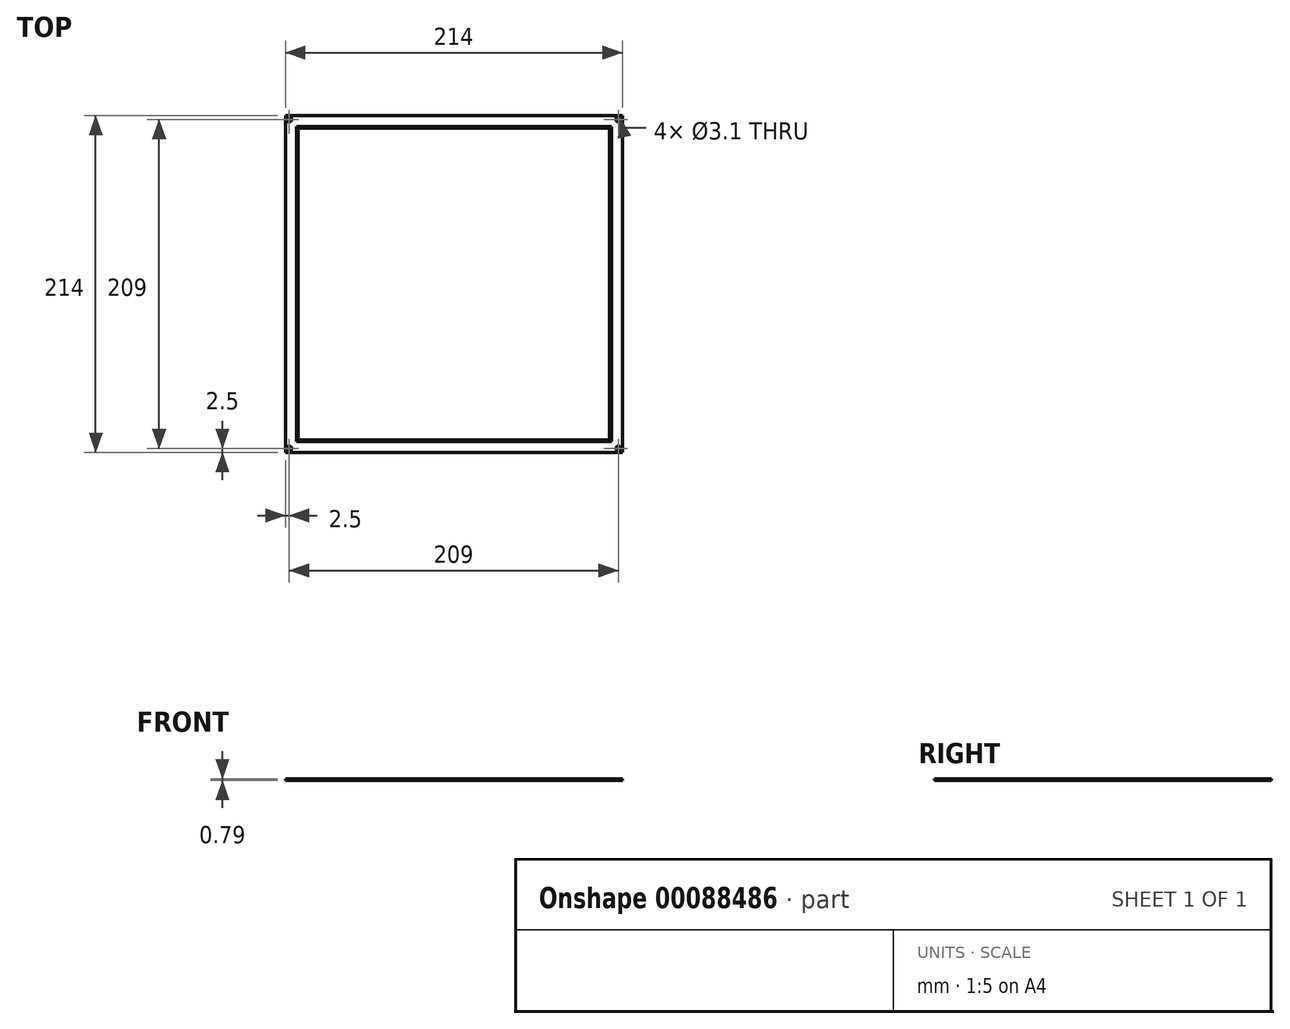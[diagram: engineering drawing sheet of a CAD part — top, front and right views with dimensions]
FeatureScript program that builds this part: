
annotation { "Feature Type Name" : "Feature", "Feature Type Description" : "" }
export const myFeature = defineFeature(function(context is Context, id is Id, definition is map)
    precondition{}
    {
        {
            var Q0;
            Q0=qCreatedBy(makeId("Top.planeOp"),FACE);
            var sketch = newSketch(context, id + "F0", { "sketchPlane" : qUnion([Q0])});
            skLineSegment(sketch, "E0.bottom", {"start": v(-107, 107) * mm, "end": v(107, 107) * mm});
            skLineSegment(sketch, "E0.top", {"start": v(-107, -107) * mm, "end": v(107, -107) * mm});
            skLineSegment(sketch, "E0.left", {"start": v(-107, 107) * mm, "end": v(-107, -107) * mm});
            skLineSegment(sketch, "E0.right", {"start": v(107, 107) * mm, "end": v(107, -107) * mm});
            skLineSegment(sketch, "E1", {"start": v(-107, 107) * mm, "end": v(107, -107) * mm, "construction": true});
            skLineSegment(sketch, "E2", {"start": v(107, 107) * mm, "end": v(-107, -107) * mm, "construction": true});
            skLineSegment(sketch, "E3.bottom", {"start": v(-104.5, 104.5) * mm, "end": v(104.5, 104.5) * mm, "construction": true});
            skLineSegment(sketch, "E3.top", {"start": v(-104.5, -104.5) * mm, "end": v(104.5, -104.5) * mm, "construction": true});
            skLineSegment(sketch, "E3.left", {"start": v(-104.5, 104.5) * mm, "end": v(-104.5, -104.5) * mm, "construction": true});
            skLineSegment(sketch, "E3.right", {"start": v(104.5, 104.5) * mm, "end": v(104.5, -104.5) * mm, "construction": true});
            skCircle(sketch, "E4", {"center": v(-104.5, 104.5) * mm, "radius": 1.55 * mm});
            skCircle(sketch, "E5", {"center": v(104.5, 104.5) * mm, "radius": 1.55 * mm});
            skCircle(sketch, "E6", {"center": v(104.5, -104.5) * mm, "radius": 1.55 * mm});
            skCircle(sketch, "E7", {"center": v(-104.5, -104.5) * mm, "radius": 1.55 * mm});
            skPoint(sketch, "E8", {"position": v(0, 0) * mm});
            skSolve(sketch);
        }
        {
            var Q0;
            Q0=makeQuery(id+"F0.imprint","IMPRINT",FACE,{"disambiguationData":[TD([[makeQuery(id+"F0.imprint","IMPRINT",EDGE,{"derivedFrom":sQuery(id+"F0.wireOp",EDGE,"E0.bottom")}),-1.0]])]});
            extrude(context, id + "F1", {"entities" : qUnion([Q0]), "depth" : 0.8 * mm});
        }
        {
            var Q0;
            Q0=makeQuery(id+"F1.opExtrude","CAP_FACE",FACE,{"disambiguationData":[OSD([sQuery(id+"F0.wireOp",EDGE,"E0.bottom"),sQuery(id+"F0.wireOp",EDGE,"E0.top"),sQuery(id+"F0.wireOp",EDGE,"E0.left"),sQuery(id+"F0.wireOp",EDGE,"E0.right"),sQuery(id+"F0.wireOp",EDGE,"E4"),sQuery(id+"F0.wireOp",EDGE,"E5"),sQuery(id+"F0.wireOp",EDGE,"E6"),sQuery(id+"F0.wireOp",EDGE,"E7")])],"isStart":false});
            var sketch = newSketch(context, id + "F2", { "sketchPlane" : qUnion([Q0])});
            skLineSegment(sketch, "E9.bottom", {"start": v(100, 100) * mm, "end": v(-100, 100) * mm});
            skLineSegment(sketch, "E9.top", {"start": v(100, -100) * mm, "end": v(-100, -100) * mm});
            skLineSegment(sketch, "E9.left", {"start": v(100, 100) * mm, "end": v(100, -100) * mm});
            skLineSegment(sketch, "E9.right", {"start": v(-100, 100) * mm, "end": v(-100, -100) * mm});
            skPoint(sketch, "E9.middle", {"position": v(0, 0) * mm});
            skLineSegment(sketch, "E10.0", {"start": v(99, 99) * mm, "end": v(-99, 99) * mm});
            skLineSegment(sketch, "E10.1", {"start": v(99, 99) * mm, "end": v(99, -99) * mm});
            skLineSegment(sketch, "E10.2", {"start": v(99, -99) * mm, "end": v(-99, -99) * mm});
            skLineSegment(sketch, "E10.3", {"start": v(-99, 99) * mm, "end": v(-99, -99) * mm});
            skSolve(sketch);
        }
        {
            var Q0;
            Q0 = qSketchRegion(id + "F2", true);
            extrude(context, id + "F3", {"entities" : qUnion([Q0]), "operationType" : NewBodyOperationType.REMOVE, "endBound" : BoundingType.SYMMETRIC, "depth" : .5 * mm});
        }
    });
